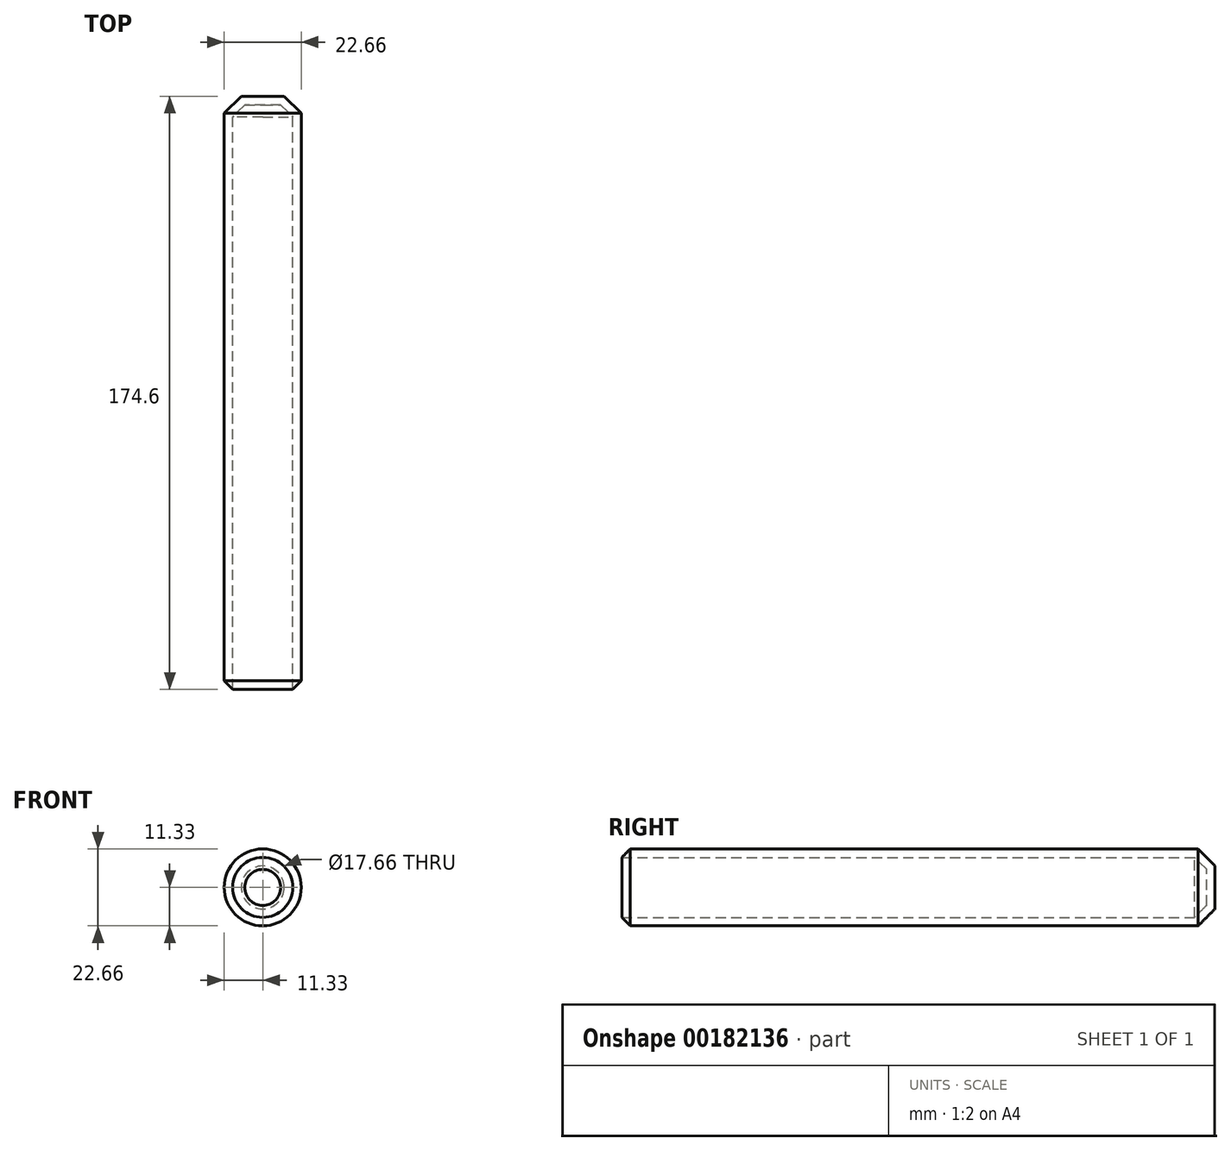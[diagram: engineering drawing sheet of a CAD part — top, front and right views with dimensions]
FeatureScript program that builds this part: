
annotation { "Feature Type Name" : "Feature", "Feature Type Description" : "" }
export const myFeature = defineFeature(function(context is Context, id is Id, definition is map)
    precondition{}
    {
        {
            var Q0;
            Q0=qCreatedBy(makeId("Front.planeOp"),FACE);
            var sketch = newSketch(context, id + "F0", { "sketchPlane" : qUnion([Q0])});
            skCircle(sketch, "E0", {"center": v(0, 0) * mm, "radius": 11.33 * mm});
            skSolve(sketch);
        }
        {
            var Q0;
            Q0 = qSketchRegion(id + "F0", true);
            extrude(context, id + "F1", {"entities" : qUnion([Q0]), "depth" : 177.1 * mm});
        }
        {
            var Q0;
            Q0=makeQuery(id+"F1.opExtrude","CAP_FACE",FACE,{"disambiguationData":[OSD([sQuery(id+"F0.wireOp",EDGE,"E0")])],"isStart":false});
            extrude(context, id + "F2", {"entities" : qUnion([Q0]), "operationType" : NewBodyOperationType.ADD, "oppositeDirection" : true, "depth" : 52.2 * mm});
        }
        {
            var Q0;
            Q0=makeQuery(id+"F1.opExtrude","CAP_EDGE",EDGE,{"disambiguationData":[OSD([sQuery(id+"F0.wireOp",EDGE,"E0")])],"isStart":false});
            var Q1;
            Q1=makeQuery(id+"F1.opExtrude","CAP_EDGE",EDGE,{"disambiguationData":[OSD([sQuery(id+"F0.wireOp",EDGE,"E0")])],"isStart":true});
            chamfer(context, id + "F3", {"entities" : qUnion([Q0, Q1]), "width" : 5 * mm, "tangentPropagation" : true});
        }
        {
            var Q0;
            Q0=makeQuery(id+"F1.opExtrude","CAP_FACE",FACE,{"disambiguationData":[OSD([sQuery(id+"F0.wireOp",EDGE,"E0")])],"isStart":false});
            var Q1;
            {var subQ0=sQuery(id+"F0.wireOp",EDGE,"E0");Q1=makeQuery(id+"F3.opChamfer","BLEND_FACE",FACE,{"disambiguationData":[OSD([subQ0]),TDD([makeQuery(id+"F1.opExtrude","CAP_EDGE",EDGE,{"disambiguationData":[OSD([subQ0])],"isStart":false})])]});}
            shell(context, id + "F4", {"entities" : qUnion([Q0, Q1]), "thickness" : 2.5 * mm});
        }
    });
